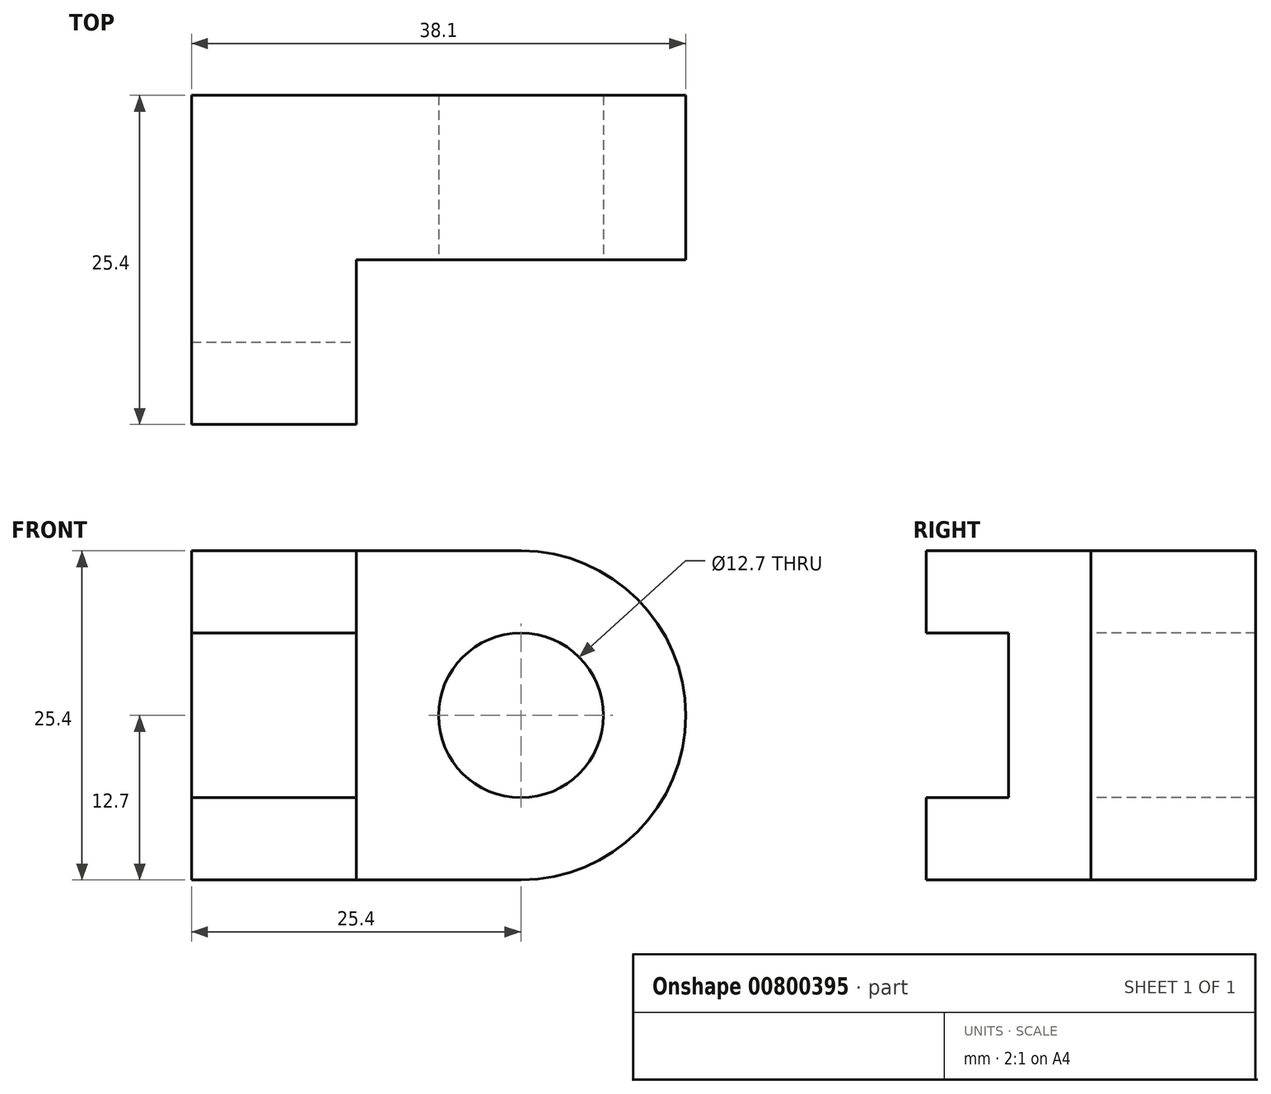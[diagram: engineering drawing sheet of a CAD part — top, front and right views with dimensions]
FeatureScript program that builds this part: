
annotation { "Feature Type Name" : "Feature", "Feature Type Description" : "" }
export const myFeature = defineFeature(function(context is Context, id is Id, definition is map)
    precondition{}
    {
        {
            var Q0;
            Q0=qCreatedBy(makeId("Top.planeOp"),FACE);
            var sketch = newSketch(context, id + "F0", { "sketchPlane" : qUnion([Q0])});
            skLineSegment(sketch, "E0", {"start": v(0, 0) * mm, "end": v(0, -25.4) * mm});
            skLineSegment(sketch, "E1", {"start": v(0, -25.4) * mm, "end": v(12.7, -25.4) * mm});
            skLineSegment(sketch, "E2", {"start": v(12.7, -25.4) * mm, "end": v(12.7, -12.7) * mm});
            skLineSegment(sketch, "E3", {"start": v(12.7, -12.7) * mm, "end": v(47, -12.7) * mm});
            skLineSegment(sketch, "E4", {"start": v(47, -12.7) * mm, "end": v(47, 0) * mm});
            skLineSegment(sketch, "E5", {"start": v(47, 0) * mm, "end": v(0, 0) * mm});
            skSolve(sketch);
        }
        {
            var Q0;
            Q0 = qSketchRegion(id + "F0", true);
            extrude(context, id + "F1", {"entities" : qUnion([Q0]), "depth" : 25.4 * mm, "offsetDistance" : 25.4 * mm});
        }
        {
            var Q0;
            Q0=makeQuery(id+"F1.opExtrude","SWEPT_FACE",FACE,{"disambiguationData":[OSD([sQuery(id+"F0.wireOp",EDGE,"E2")])]});
            var sketch = newSketch(context, id + "F2", { "sketchPlane" : qUnion([Q0])});
            skLineSegment(sketch, "E6", {"start": v(-25.4, 25.4) * mm, "end": v(-25.4, 19.05) * mm});
            skLineSegment(sketch, "E7", {"start": v(-25.4, 19.05) * mm, "end": v(-19.05, 19.05) * mm});
            skLineSegment(sketch, "E8", {"start": v(-19.05, 19.05) * mm, "end": v(-19.05, 6.35) * mm});
            skLineSegment(sketch, "E9", {"start": v(-19.05, 6.35) * mm, "end": v(-25.4, 6.35) * mm});
            skLineSegment(sketch, "E10", {"start": v(-25.4, 6.35) * mm, "end": v(-25.4, 0) * mm});
            skLineSegment(sketch, "E11", {"start": v(-25.4, 0) * mm, "end": v(-19.05, 0) * mm});
            skSolve(sketch);
        }
        {
            var Q0;
            Q0 = qSketchRegion(id + "F2", true);
            var Q1;
            {var subQ0=sQuery(id+"F2.wireOp",EDGE,"E7");Q1=makeQuery(id+"F2.imprint","IMPRINT",FACE,{"disambiguationData":[TD([[makeQuery(id+"F2.imprint","IMPRINT",EDGE,{"derivedFrom":subQ0}),-1.0]])]});}
            extrude(context, id + "F3", {"entities" : qUnion([Q0, Q1]), "operationType" : NewBodyOperationType.REMOVE, "endBound" : BoundingType.THROUGH_ALL, "oppositeDirection" : true, "depth" : 25.4 * mm, "offsetDistance" : 25.4 * mm});
        }
        {
            var Q0;
            Q0=makeQuery(id+"F1.opExtrude","SWEPT_FACE",FACE,{"disambiguationData":[OSD([sQuery(id+"F0.wireOp",EDGE,"E3")])]});
            var sketch = newSketch(context, id + "F4", { "sketchPlane" : qUnion([Q0])});
            skLineSegment(sketch, "E12", {"start": v(12.7, 25.4) * mm, "end": v(25.4, 25.4) * mm});
            skLineSegment(sketch, "E13", {"start": v(12.7, 0) * mm, "end": v(25.4, 0) * mm});
            skArc(sketch, "E14", {"start": v(25.4, 0) * mm, "mid": v(38.1, 12.7) * mm, "end": v(25.4, 25.4) * mm});
            skLineSegment(sketch, "E15", {"start": v(25.4, 25.4) * mm, "end": v(25.4, 19.05) * mm, "construction": true});
            skLineSegment(sketch, "E16", {"start": v(25.4, 0) * mm, "end": v(25.4, 6.35) * mm, "construction": true});
            skCircle(sketch, "E17", {"center": v(25.4, 12.7) * mm, "radius": 6.35 * mm});
            skSolve(sketch);
        }
        {
            var Q0;
            {var subQ0=sQuery(id+"F4.wireOp",EDGE,"E14");Q0=makeQuery(id+"F4.imprint","IMPRINT",FACE,{"disambiguationData":[TD([[makeQuery(id+"F4.imprint","IMPRINT",EDGE,{"derivedFrom":subQ0}),-1.0]])]});}
            var Q1;
            Q1=makeQuery(id+"F4.imprint","IMPRINT",FACE,{"disambiguationData":[TD([[makeQuery(id+"F4.imprint","IMPRINT",EDGE,{"derivedFrom":sQuery(id+"F4.wireOp",EDGE,"E17")}),1.0]])]});
            extrude(context, id + "F5", {"entities" : qUnion([Q0, Q1]), "operationType" : NewBodyOperationType.REMOVE, "endBound" : BoundingType.THROUGH_ALL, "oppositeDirection" : true, "depth" : 25.4 * mm, "offsetDistance" : 25.4 * mm});
        }
    });
